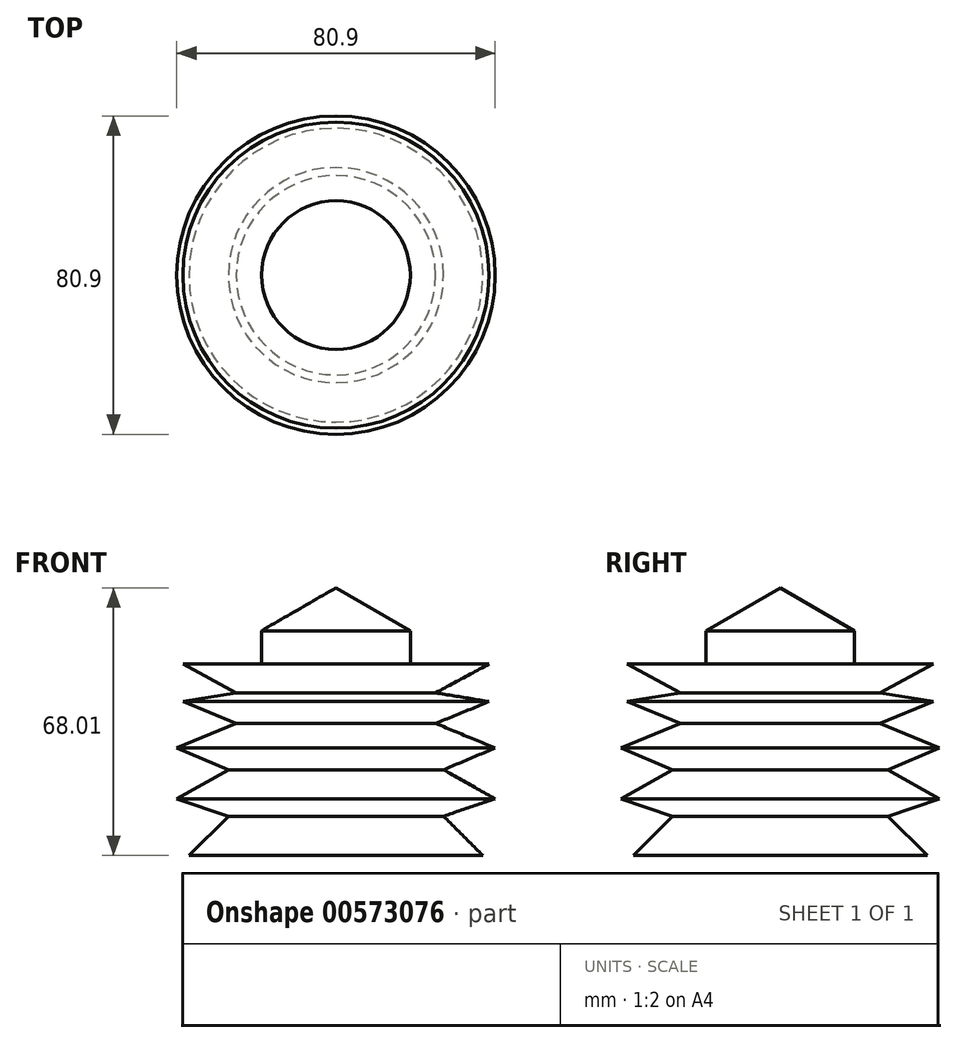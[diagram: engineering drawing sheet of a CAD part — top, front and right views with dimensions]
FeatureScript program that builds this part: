
annotation { "Feature Type Name" : "Feature", "Feature Type Description" : "" }
export const myFeature = defineFeature(function(context is Context, id is Id, definition is map)
    precondition{}
    {
        {
            var Q0;
            Q0=qCreatedBy(makeId("Front.planeOp"),FACE);
            var sketch = newSketch(context, id + "F0", { "sketchPlane" : qUnion([Q0])});
            skLineSegment(sketch, "E0", {"start": v(-37.34, 0) * mm, "end": v(-27.34, 10) * mm});
            skLineSegment(sketch, "E1", {"start": v(-27.34, 10) * mm, "end": v(-40.45, 14.45) * mm});
            skLineSegment(sketch, "E2", {"start": v(-40.45, 14.45) * mm, "end": v(-27.34, 21.78) * mm});
            skLineSegment(sketch, "E3", {"start": v(-27.34, 21.78) * mm, "end": v(-40.45, 27.34) * mm});
            skLineSegment(sketch, "E4", {"start": v(-40.45, 27.34) * mm, "end": v(-25.34, 33.56) * mm});
            skLineSegment(sketch, "E5", {"start": v(-25.34, 33.56) * mm, "end": v(-38.9, 39.12) * mm});
            skLineSegment(sketch, "E6", {"start": v(-38.9, 39.12) * mm, "end": v(-25.34, 41.34) * mm});
            skLineSegment(sketch, "E7", {"start": v(-25.34, 41.34) * mm, "end": v(-38.9, 48.67) * mm});
            skLineSegment(sketch, "E8", {"start": v(-38.9, 48.67) * mm, "end": v(-18.9, 48.67) * mm});
            skLineSegment(sketch, "E9", {"start": v(-18.9, 48.67) * mm, "end": v(-18.9, 57.12) * mm});
            skLineSegment(sketch, "E10", {"start": v(-18.9, 57.12) * mm, "end": v(0, 68) * mm});
            skLineSegment(sketch, "E11", {"start": v(0, 68) * mm, "end": v(0, 0) * mm});
            skLineSegment(sketch, "E12", {"start": v(0, 0) * mm, "end": v(-37.34, 0) * mm});
            skSolve(sketch);
        }
        {
            var Q0;
            Q0=makeQuery(id+"F0.imprint","IMPRINT",FACE,{"disambiguationData":[TD([[makeQuery(id+"F0.imprint","IMPRINT",EDGE,{"derivedFrom":sQuery(id+"F0.wireOp",EDGE,"E0")}),-1.0]])]});
            var Q1;
            Q1=sQuery(id+"F0.wireOp",EDGE,"E11");
            revolve(context, id + "F1", {"entities" : qUnion([Q0]), "axis" : qUnion([Q1]), "revolveType" : RevolveType.FULL});
        }
    });
